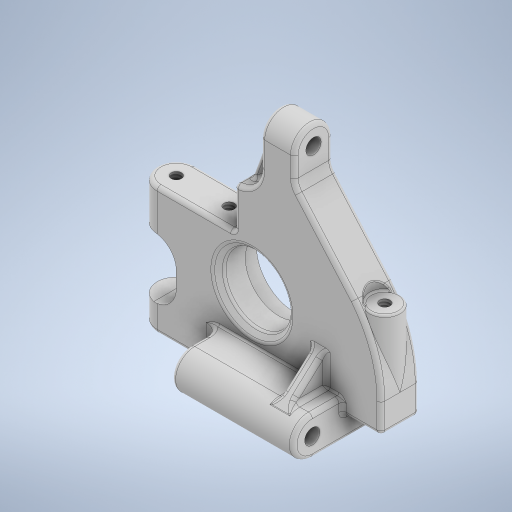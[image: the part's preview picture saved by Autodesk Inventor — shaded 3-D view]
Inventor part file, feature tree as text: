
AUTODESK INVENTOR PART (.ipt)
format: ipt  version: 2024 (Build 280153000, 153)  size: 1,162,240 bytes
history: native  units: in
note: dims shown in document units (in); Inventor stores cm internally (conversion verified against a paired STEP export)
features: fillet x19, sketch x19, extrude x13, plane x8, projected_geometry x6, hole x4, other x3, rib x2, chamfer x1, direct_edit x1
ambient origin geometry x8: Origin, YZ Plane, XZ Plane, XY Plane, X Axis, Y Axis, Z Axis, Center Point
bodies: Solid1 (feature_tree)
feature tree (76):
  extrude  "Extrusion1"  Depth=0.215in
  extrude  "Extrusion2"  Depth=0.5in
  fillet  "Fillet1"  Radius=0.315in
  extrude  "Extrusion3"  Depth=0.425in
  extrude  "Extrusion4"  Depth=1.825in
  extrude  "Extrusion5"  TaperAngle=120.0deg  [1 undecoded]
  extrude  "Extrusion6"  Depth=1.0in
  extrude  "Extrusion7"  Depth=0.315in TaperAngle=0.0deg
  fillet  "Fillet2"  Radius=0.315in
  extrude  "Extrusion8"  TaperAngle=0.0deg  [1 undecoded]
  chamfer  "Chamfer1"  Distance=0.315in
  fillet  "Fillet3"  Radius=0.276in
  fillet  "Fillet4"  Radius=0.315in
  fillet  "Fillet5"  Radius=0.75in
  fillet  "Fillet6"  Radius=0.6825in
  fillet  "Fillet7"  Radius=1.0625in
  fillet  "Fillet8"  Radius=0.035in
  fillet  "Fillet9"  Radius=0.625in
  other  "Work Point1"
  plane  "Work Plane1"
  other  "Work Axis1"
  plane  "Work Plane5"
  extrude  "Extrusion9"  Depth=0.032in
  fillet  "Fillet10"  Radius=0.55in
  fillet  "Fillet11"  [1 undecoded]
  fillet  "Fillet12"  Radius=0.1875in
  fillet  "Fillet13"  Radius=0.032in
  hole  "Hole1"  [1 undecoded]
  plane  "Work Plane6"
  rib  "Rib1"
  fillet  "Fillet14"  Radius=0.032in
  plane  "Work Plane7"
  extrude  "Extrusion10"  Depth=0.032in
  extrude  "Extrusion11"  [1 undecoded]
  fillet  "Fillet15"  [1 undecoded]
  hole  "Hole2"  [1 undecoded]
  plane  "Work Plane8"
  rib  "Rib2"
  fillet  "Fillet16"  Radius=1.0in
  fillet  "Fillet17"  Radius=0.032in
  fillet  "Fillet18"  Radius=0.125in
  extrude  "Extrusion12"  Depth=0.015in
  extrude  "Extrusion13"  [1 undecoded]
  fillet  "Fillet19"  Radius=0.1in
  hole  "Hole3"  [1 undecoded]
  hole  "Hole4"  [1 undecoded]
  direct_edit  "Direct Edit1"
  sketch  "Sketch1"  dims[d0=2.0in d1=0.215in]
  sketch  "Sketch2"  dims[d2=0.315in d3=0.5in d4=0.315in]
  sketch  "Sketch3"  dims[d5=1.05in d6=0.425in]
  sketch  "Sketch4"  dims[d7=0.2762in d8=1.825in]
  sketch  "Sketch5"  dims[d9=0.361in d10=120.0deg]
  sketch  "Sketch6"  dims[d11=0.3356in d12=1.0in]
  sketch  "Sketch7"  dims[d13=0.989in d14=0.315in d15=0.0in d16=0.315in]
  sketch  "Sketch8"  dims[d17=0.1875in d18=0.0in d19=0.0in]
  plane  "Work Plane2"
  plane  "Work Plane3"
  plane  "Work Plane4"
  sketch  "Sketch10"  dims[d20=0.1575in]
  sketch  "Sketch11"  dims[d21=0.795in]
  sketch  "Sketch12"  dims[d22=0.3438in d23=0.315in d24=0.0in d25=0.276in d26=0.0in d27=0.315in d28=0.0in d29=0.75in d30=0.6825in d31=1.0625in d32=0.035in d33=0.0in d34=0.625in]
  sketch  "Sketch13"  dims[d35=0.1288in d36=0.0in d37=0.032in d38=0.55in d39=0.0in d40=0.0in]
  sketch  "Sketch14"  dims[d41=0.05in d42=0.125in d43=45.0deg d44=0.1875in d45=0.032in]
  sketch  "Sketch16"  dims[d46=0.032in d47=0.125in d48=0.032in]
  sketch  "Sketch17"  dims[d49=0.015in d50=0.032in]
  sketch  "Sketch18"  dims[d51=0.25in d52=-0.1575in d53=-1.0in]
  sketch  "Sketch19"  dims[d54=0.315in d55=0.25in d56=1.0in d57=0.0in d58=0.032in d59=0.125in]
  sketch  "Sketch20"  dims[d60=0.032in d61=0.015in]
  sketch  "Sketch21"  dims[d62=0.125in d63=0.75in d64=0.375in d65=0.25in d66=0.5635in d67=0.7874in d68=0.8108in d69=-0.5in d70=0.1in d71=0.1in d72=0.0in d73=0.0in d74=0.1in d75=0.1in d76=0.032in d77=-1.0in d78=0.25in d79=1.0in d80=0.0in d81=0.25in d82=0.0in d83=0.0in d84=0.015in d85=0.0849in d86=0.224in d87=0.375in d88=0.25in d89=0.5635in d90=0.315in d91=0.8108in d92=0.1in d93=0.1in d94=0.0in d95=0.0in d96=0.1in d97=0.1in d98=0.032in d99=0.032in d100=0.032in d101=0.22in d102=1.0in d103=0.0in d104=0.15in d105=0.0in d106=0.015in d107=0.125in d108=0.224in d109=0.375in d110=0.25in d111=0.5635in d112=0.349in d113=0.8108in d114=0.435in d115=0.0849in d116=0.224in d117=0.375in d118=0.25in d119=0.5635in d120=0.315in d121=0.8108in d122=3.937in d123=0.3937in d124=0.3937in]
  projected_geometry  "Project Cut Edges1"
  projected_geometry  "Project Cut Edges2"
  projected_geometry  "Project Cut Edges3"
  projected_geometry  "Project Cut Edges4"
  projected_geometry  "Project Cut Edges5"
  projected_geometry  "Project Cut Edges6"
  other  "Scale1"
note: 10 required parameter values undecoded (feature->parameter linkage not recoverable at this tier; creation-order binding heuristic only, values carry confidence <= 0.55)
